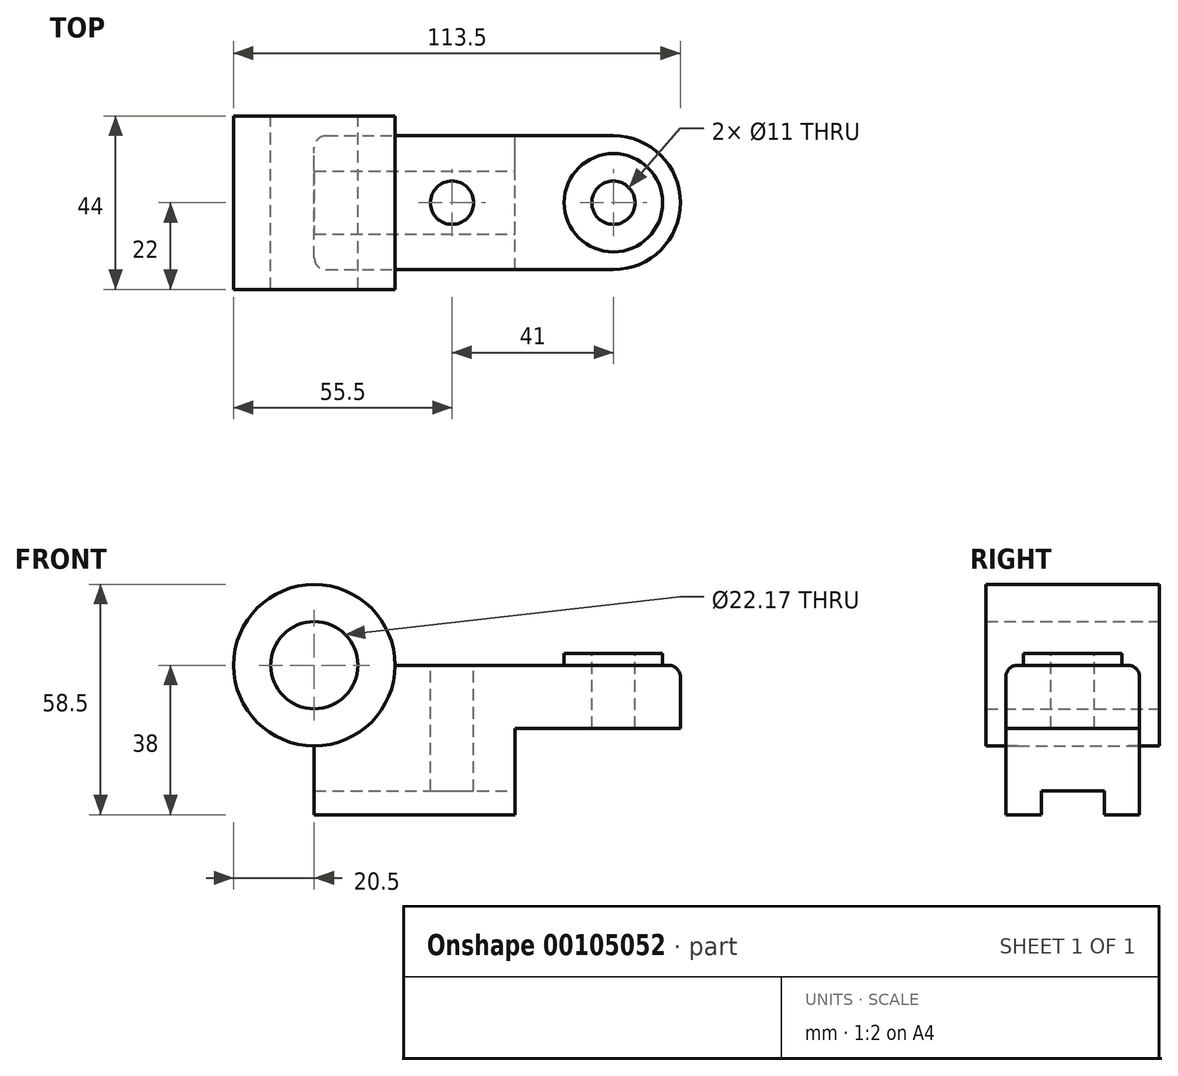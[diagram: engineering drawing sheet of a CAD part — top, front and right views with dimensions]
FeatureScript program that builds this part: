
annotation { "Feature Type Name" : "Feature", "Feature Type Description" : "" }
export const myFeature = defineFeature(function(context is Context, id is Id, definition is map)
    precondition{}
    {
        {
            var Q0;
            Q0=qCreatedBy(makeId("Front.planeOp"),FACE);
            var sketch = newSketch(context, id + "F0", { "sketchPlane" : qUnion([Q0])});
            skLineSegment(sketch, "E0.bottom", {"start": v(0, 0) * mm, "end": v(51, 0) * mm});
            skLineSegment(sketch, "E0.top", {"start": v(0, 38) * mm, "end": v(76, 38) * mm});
            skLineSegment(sketch, "E0.left", {"start": v(0, 0) * mm, "end": v(0, 38) * mm});
            skLineSegment(sketch, "E0.right", {"start": v(76, 22) * mm, "end": v(76, 38) * mm});
            skLineSegment(sketch, "E1.top", {"start": v(76, 22) * mm, "end": v(51, 22) * mm});
            skLineSegment(sketch, "E1.right", {"start": v(51, 0) * mm, "end": v(51, 22) * mm});
            skCircle(sketch, "E2", {"center": v(0, 38) * mm, "radius": 11.09 * mm});
            skCircle(sketch, "E3", {"center": v(0, 38) * mm, "radius": 20.5 * mm});
            skSolve(sketch);
        }
        {
            var Q0;
            {var subQ2=sQuery(id+"F0.wireOp",EDGE,"E0.bottom");Q0=makeQuery(id+"F0.imprint","IMPRINT",FACE,{"disambiguationData":[TD([[makeQuery(id+"F0.imprint","IMPRINT",EDGE,{"derivedFrom":subQ2}),1.0]])]});}
            extrude(context, id + "F1", {"entities" : qUnion([Q0]), "endBound" : BoundingType.SYMMETRIC, "depth" : 34 * mm});
        }
        {
            var Q0;
            Q0=qCreatedBy(makeId("Front.planeOp"),FACE);
            var sketch = newSketch(context, id + "F2", { "sketchPlane" : qUnion([Q0])});
            skSolve(sketch);
        }
        {
            var Q0;
            Q0 = qSketchRegion(id + "F2", true);
            var Q1;
            {var subQ0=sQuery(id+"F0.wireOp",EDGE,"E3");var subQ1=sQuery(id+"F0.wireOp",EDGE,"E0.top");var subQ2=makeQuery(id+"F0.imprint","INTERSECT",VERTEX,{"derivedFrom":[subQ1,subQ0]});Q1=makeQuery(id+"F0.imprint","IMPRINT",FACE,{"disambiguationData":[TD([[makeQuery(id+"F0.imprint","IMPRINT",EDGE,{"disambiguationData":[TD([[subQ2,1.0]])],"derivedFrom":subQ1}),1.0]])]});}
            var Q2;
            {var subQ0=sQuery(id+"F0.wireOp",EDGE,"E3");var subQ1=sQuery(id+"F0.wireOp",EDGE,"E0.top");var subQ2=makeQuery(id+"F0.imprint","INTERSECT",VERTEX,{"derivedFrom":[subQ1,subQ0]});Q2=makeQuery(id+"F0.imprint","IMPRINT",FACE,{"disambiguationData":[TD([[makeQuery(id+"F0.imprint","IMPRINT",EDGE,{"disambiguationData":[TD([[subQ2,1.0]])],"derivedFrom":subQ1}),-1.0]])]});}
            extrude(context, id + "F3", {"entities" : qUnion([Q0, Q1, Q2]), "operationType" : NewBodyOperationType.ADD, "endBound" : BoundingType.SYMMETRIC, "depth" : 44 * mm});
        }
        {
            var Q0;
            Q0=makeQuery(id+"F1.opExtrude","SWEPT_FACE",FACE,{"disambiguationData":[OSD([sQuery(id+"F0.wireOp",EDGE,"E0.top")])]});
            var sketch = newSketch(context, id + "F4", { "sketchPlane" : qUnion([Q0])});
            skArc(sketch, "E4", {"start": v(76, -17) * mm, "mid": v(93, 0) * mm, "end": v(76, 17) * mm});
            skSolve(sketch);
        }
        {
            var Q0;
            Q0 = qSketchRegion(id + "F4", true);
            var Q1;
            Q1=makeQuery(id+"F4.imprint","IMPRINT",FACE,{"disambiguationData":[TD([[makeQuery(id+"F4.imprint","IMPRINT",EDGE,{"derivedFrom":sQuery(id+"F4.wireOp",EDGE,"E4")}),1.0]])]});
            var Q2;
            Q2=makeQuery(id+"F1.opExtrude","SWEPT_FACE",FACE,{"disambiguationData":[OSD([sQuery(id+"F0.wireOp",EDGE,"E1.top")])]});
            extrude(context, id + "F5", {"entities" : qUnion([Q0, Q1]), "operationType" : NewBodyOperationType.ADD, "endBound" : BoundingType.UP_TO_SURFACE, "oppositeDirection" : true, "endBoundEntityFace" : qUnion([Q2]), "depth" : 25 * mm});
        }
        {
            var Q0;
            {var subQ0=sQuery(id+"F0.wireOp",EDGE,"E0.top");Q0=makeQuery(id+"F5.boolean.opBoolean","MERGE",FACE,{"derivedFrom":[makeQuery(id+"F1.opExtrude","SWEPT_FACE",FACE,{"disambiguationData":[OSD([subQ0])]}),makeQuery(id+"F5.opExtrude","CAP_FACE",FACE,{"disambiguationData":[OSD([subQ0,sQuery(id+"F0.wireOp",EDGE,"E0.right"),sQuery(id+"F4.wireOp",EDGE,"E4")])],"isStart":true})]});}
            var sketch = newSketch(context, id + "F6", { "sketchPlane" : qUnion([Q0])});
            skCircle(sketch, "E5", {"center": v(76, 0) * mm, "radius": 12.5 * mm});
            skSolve(sketch);
        }
        {
            var Q0;
            Q0=makeQuery(id+"F6.imprint","IMPRINT",FACE,{"disambiguationData":[TD([[makeQuery(id+"F6.imprint","IMPRINT",EDGE,{"derivedFrom":sQuery(id+"F6.wireOp",EDGE,"E5")}),1.0]])]});
            extrude(context, id + "F7", {"entities" : qUnion([Q0]), "operationType" : NewBodyOperationType.ADD, "depth" : 3 * mm});
        }
        {
            var Q0;
            Q0=makeQuery(id+"F7.opExtrude","CAP_FACE",FACE,{"disambiguationData":[OSD([sQuery(id+"F6.wireOp",EDGE,"E5")])],"isStart":false});
            var sketch = newSketch(context, id + "F8", { "sketchPlane" : qUnion([Q0])});
            skCircle(sketch, "E6", {"center": v(76, 0) * mm, "radius": 5.5 * mm});
            skCircle(sketch, "E7", {"center": v(35, 0) * mm, "radius": 5.5 * mm});
            skSolve(sketch);
        }
        {
            var Q0;
            Q0 = qSketchRegion(id + "F8", true);
            extrude(context, id + "F9", {"entities" : qUnion([Q0]), "operationType" : NewBodyOperationType.REMOVE, "endBound" : BoundingType.THROUGH_ALL, "oppositeDirection" : true, "depth" : 25 * mm});
        }
        {
            var Q0;
            Q0=makeQuery(id+"F1.opExtrude","SWEPT_FACE",FACE,{"disambiguationData":[OSD([sQuery(id+"F0.wireOp",EDGE,"E1.right")])]});
            var sketch = newSketch(context, id + "F10", { "sketchPlane" : qUnion([Q0])});
            skLineSegment(sketch, "E8.bottom", {"start": v(-8, 0) * mm, "end": v(8, 0) * mm});
            skLineSegment(sketch, "E8.top", {"start": v(-8, 6) * mm, "end": v(8, 6) * mm});
            skLineSegment(sketch, "E8.left", {"start": v(-8, 0) * mm, "end": v(-8, 6) * mm});
            skLineSegment(sketch, "E8.right", {"start": v(8, 0) * mm, "end": v(8, 6) * mm});
            skSolve(sketch);
        }
        {
            var Q0;
            Q0=makeQuery(id+"F10.imprint","IMPRINT",FACE,{"disambiguationData":[TD([[makeQuery(id+"F10.imprint","IMPRINT",EDGE,{"derivedFrom":sQuery(id+"F10.wireOp",EDGE,"E8.bottom")}),1.0]])]});
            extrude(context, id + "F11", {"entities" : qUnion([Q0]), "operationType" : NewBodyOperationType.REMOVE, "endBound" : BoundingType.THROUGH_ALL, "oppositeDirection" : true, "depth" : 25 * mm});
        }
        {
            var Q0;
            Q0=makeQuery(id+"F7.opExtrude","CAP_EDGE",EDGE,{"disambiguationData":[OSD([sQuery(id+"F6.wireOp",EDGE,"E5")])],"isStart":true});
            var Q1;
            Q1=makeQuery(id+"F1.opExtrude","SWEPT_EDGE",EDGE,{"disambiguationData":[OSD([sQuery(id+"F0.wireOp",EDGE,"E0.top"),sQuery(id+"F0.wireOp",EDGE,"E3")])]});
            var Q2;
            Q2=makeQuery(id+"F1.opExtrude","CAP_EDGE",EDGE,{"disambiguationData":[OSD([sQuery(id+"F0.wireOp",EDGE,"E3")])],"isStart":false});
            var Q3;
            Q3=makeQuery(id+"F1.opExtrude","CAP_EDGE",EDGE,{"disambiguationData":[OSD([sQuery(id+"F0.wireOp",EDGE,"E3")])],"isStart":true});
            var Q4;
            Q4=makeQuery(id+"F1.opExtrude","SWEPT_EDGE",EDGE,{"disambiguationData":[OSD([sQuery(id+"F0.wireOp",EDGE,"E0.left"),sQuery(id+"F0.wireOp",EDGE,"E3")])]});
            var Q5;
            Q5=makeQuery(id+"F1.opExtrude","CAP_EDGE",EDGE,{"disambiguationData":[OSD([sQuery(id+"F0.wireOp",EDGE,"E0.left")])],"isStart":false});
            var Q6;
            Q6=makeQuery(id+"F1.opExtrude","CAP_EDGE",EDGE,{"disambiguationData":[OSD([sQuery(id+"F0.wireOp",EDGE,"E0.left")])],"isStart":true});
            fillet(context, id + "F12", {"entities" : qUnion([Q0, Q1, Q2, Q3, Q4, Q5, Q6]), "radius" : 3 * mm, "tangentPropagation" : true, "allowEdgeOverflow" : false});
        }
        {
            var Q0;
            Q0=makeQuery(id+"F1.opExtrude","CAP_EDGE",EDGE,{"disambiguationData":[OSD([sQuery(id+"F0.wireOp",EDGE,"E0.top")])],"isStart":false});
            fillet(context, id + "F13", {"entities" : qUnion([Q0]), "radius" : 3 * mm, "tangentPropagation" : true, "allowEdgeOverflow" : false});
        }
    });
